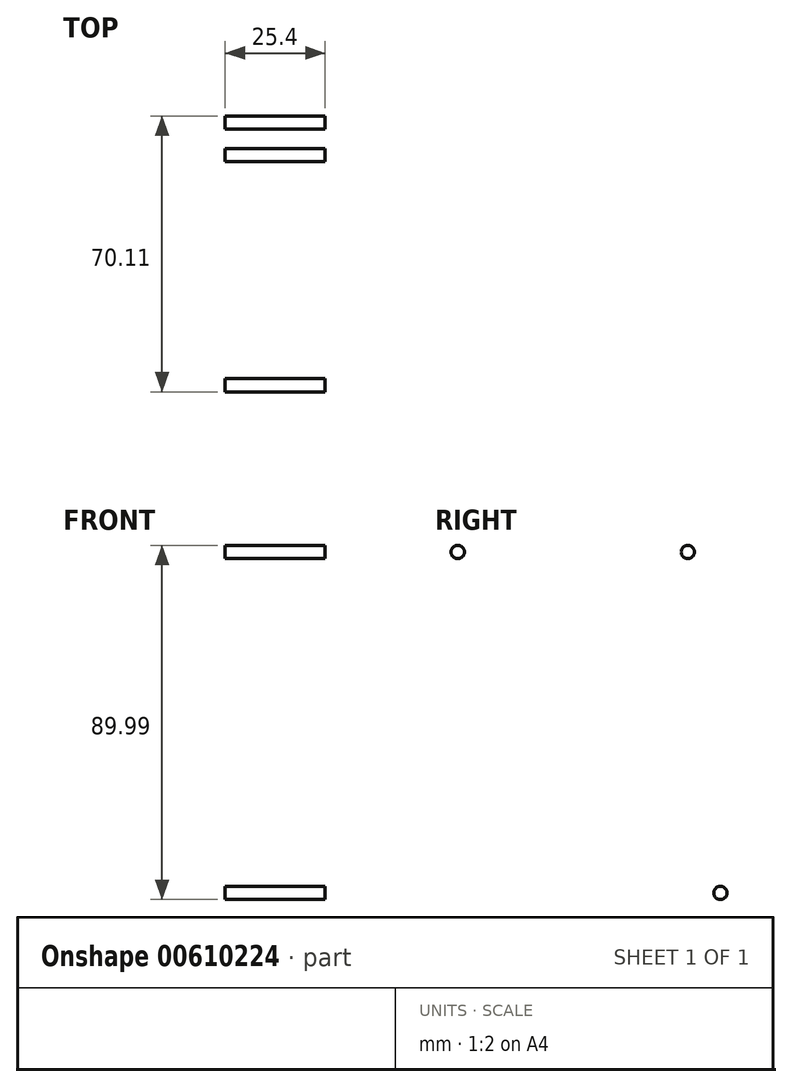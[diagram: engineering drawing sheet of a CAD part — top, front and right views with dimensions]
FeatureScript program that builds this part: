
annotation { "Feature Type Name" : "Feature", "Feature Type Description" : "" }
export const myFeature = defineFeature(function(context is Context, id is Id, definition is map)
    precondition{}
    {
        {
            var Q0;
            Q0=qCreatedBy(makeId("Right.planeOp"),FACE);
            cPlane(context, id + "F0", {"entities" : qUnion([Q0]), "cplaneType" : CPlaneType.OFFSET, "offset" : 25.4 * mm, "width" : 152.4 * mm, "height" : 152.4 * mm});
        }
        {
            var Q0;
            Q0=qCreatedBy(makeId("Right.planeOp"),FACE);
            var sketch = newSketch(context, id + "F1", { "sketchPlane" : qUnion([Q0])});
            skLineSegment(sketch, "E0", {"start": v(0, 28.3) * mm, "end": v(15.47, -31.98) * mm});
            skLineSegment(sketch, "E1", {"start": v(-61.81, 32.5) * mm, "end": v(-58.45, 28.3) * mm});
            skLineSegment(sketch, "E2", {"start": v(-58.45, 28.3) * mm, "end": v(4.42, 28.3) * mm});
            skLineSegment(sketch, "E3", {"start": v(-23.72, -55.17) * mm, "end": v(8.28, -58.32) * mm});
            skLineSegment(sketch, "E4", {"start": v(8.28, -3.95) * mm, "end": v(8.28, -58.32) * mm});
            skCircle(sketch, "E5", {"center": v(8.28, -58.32) * mm, "radius": 1.69 * mm});
            skCircle(sketch, "E6", {"center": v(-58.45, 28.3) * mm, "radius": 1.69 * mm});
            skCircle(sketch, "E7", {"center": v(0, 28.3) * mm, "radius": 1.69 * mm});
            skLineSegment(sketch, "E8", {"start": v(4.42, 28.3) * mm, "end": v(7.44, 32.5) * mm});
            skCircle(sketch, "E9", {"center": v(14.75, -55.08) * mm, "radius": 10.54 * mm, "construction": true});
            skLineSegment(sketch, "E10", {"start": v(-23.72, -55.17) * mm, "end": v(-26.03, -58.41) * mm});
            skSolve(sketch);
        }
        {
            var Q0;
            Q0=qCreatedBy(makeId("Front.planeOp"),FACE);
            var sketch = newSketch(context, id + "F2", { "sketchPlane" : qUnion([Q0])});
            skCircle(sketch, "E11", {"center": v(0, -55.17) * mm, "radius": 1.69 * mm});
            skCircle(sketch, "E12", {"center": v(0, 28.3) * mm, "radius": 1.69 * mm});
            skCircle(sketch, "E13", {"center": v(25.2, 28.3) * mm, "radius": 1.69 * mm});
            skCircle(sketch, "E14", {"center": v(25.2, -55.17) * mm, "radius": 1.69 * mm});
            skCircle(sketch, "E15", {"center": v(25.3, -15.17) * mm, "radius": 1.69 * mm});
            skSolve(sketch);
        }
        {
            var Q0;
            Q0=sQuery(id+"F1.wireOp",EDGE,"QTojlz1a-oFvP-hQNg-EAAu-UZ7DLm6qaUf1");
            var Q1;
            Q1=sQuery(id+"F1.wireOp",EDGE,"E6");
            var Q2;
            Q2=sQuery(id+"F1.wireOp",EDGE,"E5");
            var Q3;
            Q3=sQuery(id+"F1.wireOp",EDGE,"E7");
            extrude(context, id + "F3", {"bodyType" : ToolBodyType.SURFACE, "surfaceEntities" : qUnion([Q0, Q1, Q2, Q3]), "depth" : 25.4 * mm, "offsetDistance" : 25.4 * mm});
        }
        {
            var Q0;
            Q0=qCreatedBy(makeId("Top.planeOp"),FACE);
            var sketch = newSketch(context, id + "F4", { "sketchPlane" : qUnion([Q0])});
            skCircle(sketch, "E16", {"center": v(16.08, 11.78) * mm, "radius": 1.91 * mm});
            skCircle(sketch, "E17", {"center": v(8.03, 11.78) * mm, "radius": 1.91 * mm});
            skCircle(sketch, "E18", {"center": v(17.08, 5.54) * mm, "radius": 1.91 * mm});
            skCircle(sketch, "E19", {"center": v(9.03, 5.54) * mm, "radius": 1.91 * mm});
            skSolve(sketch);
        }
    });
